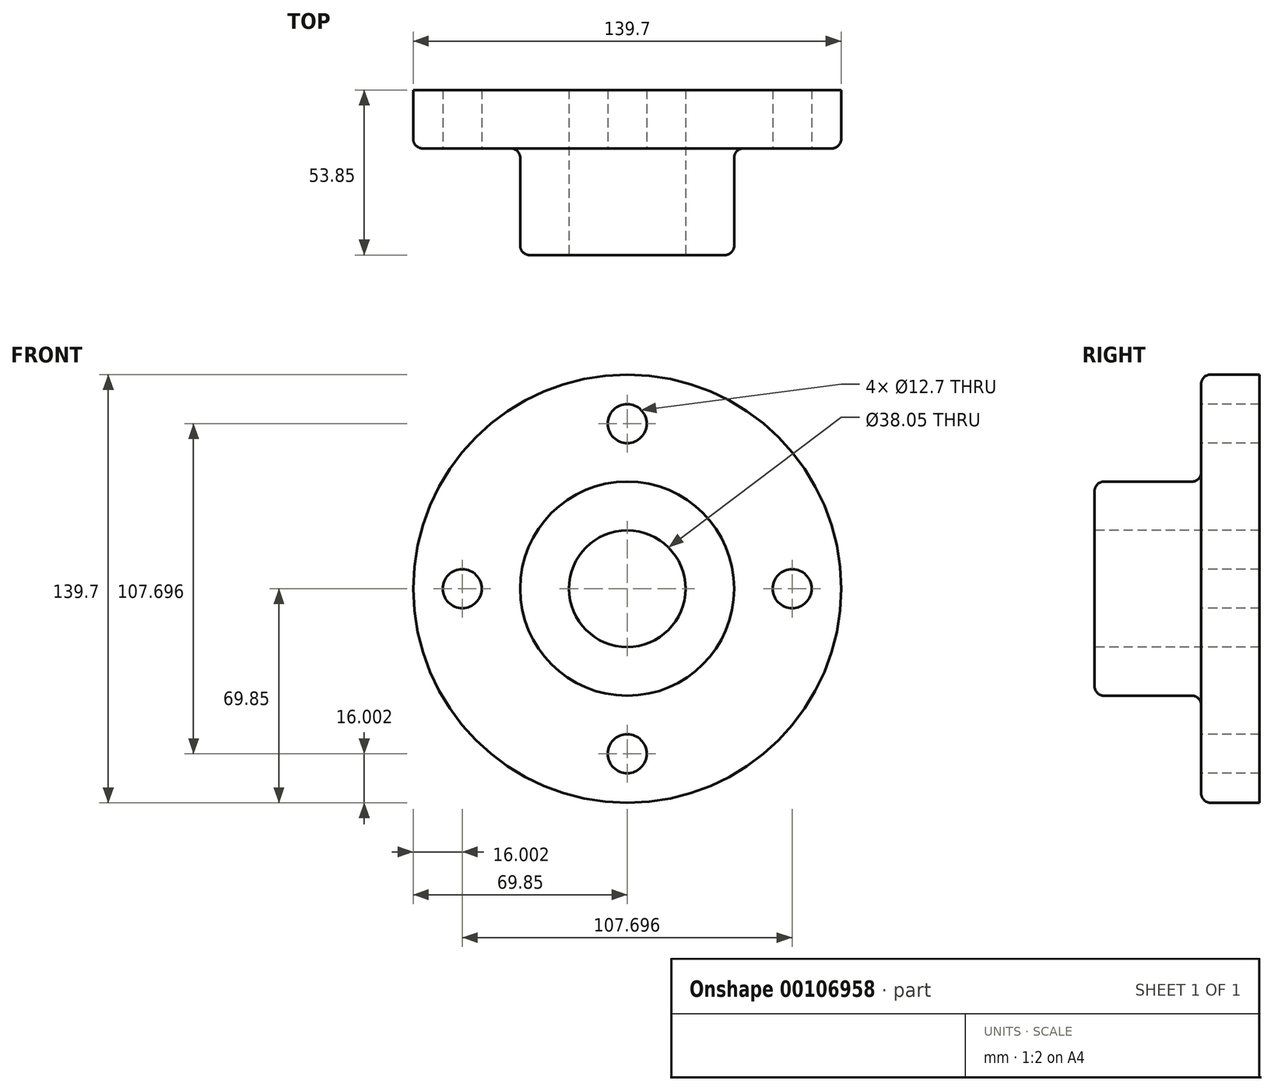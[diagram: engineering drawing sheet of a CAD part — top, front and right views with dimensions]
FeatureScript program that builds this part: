
annotation { "Feature Type Name" : "Feature", "Feature Type Description" : "" }
export const myFeature = defineFeature(function(context is Context, id is Id, definition is map)
    precondition{}
    {
        {
            var Q0;
            Q0=qCreatedBy(makeId("Right.planeOp"),FACE);
            var sketch = newSketch(context, id + "F0", { "sketchPlane" : qUnion([Q0])});
            skLineSegment(sketch, "E0", {"start": v(0, 0) * mm, "end": v(53.85, 0) * mm});
            skLineSegment(sketch, "E1", {"start": v(53.85, 0) * mm, "end": v(53.85, 69.85) * mm});
            skLineSegment(sketch, "E2", {"start": v(53.85, 69.85) * mm, "end": v(34.8, 69.85) * mm});
            skLineSegment(sketch, "E3", {"start": v(34.8, 69.85) * mm, "end": v(34.8, 34.93) * mm});
            skLineSegment(sketch, "E4", {"start": v(34.8, 34.93) * mm, "end": v(0, 34.93) * mm});
            skLineSegment(sketch, "E5", {"start": v(0, 34.93) * mm, "end": v(0, 0) * mm});
            skSolve(sketch);
        }
        {
            var Q0;
            Q0=makeQuery(id+"F0.imprint","IMPRINT",FACE,{"disambiguationData":[TD([[makeQuery(id+"F0.imprint","IMPRINT",EDGE,{"derivedFrom":sQuery(id+"F0.wireOp",EDGE,"E0")}),1.0]])]});
            var Q1;
            Q1=sQuery(id+"F0.wireOp",EDGE,"E0");
            revolve(context, id + "F1", {"entities" : qUnion([Q0]), "axis" : qUnion([Q1]), "revolveType" : RevolveType.FULL});
        }
        {
            var Q0;
            Q0=makeQuery(id+"F1.opRevolve","SWEPT_FACE",FACE,{"disambiguationData":[OSD([sQuery(id+"F0.wireOp",EDGE,"E5")])]});
            var sketch = newSketch(context, id + "F2", { "sketchPlane" : qUnion([Q0])});
            skCircle(sketch, "E6", {"center": v(0, 0) * mm, "radius": 19.02 * mm});
            skSolve(sketch);
        }
        {
            var Q0;
            Q0 = qSketchRegion(id + "F2", true);
            var Q1;
            Q1 = qSketchRegion(id + "F4", true);
            extrude(context, id + "F3", {"entities" : qUnion([Q0, Q1]), "operationType" : NewBodyOperationType.REMOVE, "endBound" : BoundingType.THROUGH_ALL, "oppositeDirection" : true, "depth" : 25 * mm});
        }
        {
            var Q0;
            Q0=makeQuery(id+"F1.opRevolve","SWEPT_FACE",FACE,{"disambiguationData":[OSD([sQuery(id+"F0.wireOp",EDGE,"E3")])]});
            var sketch = newSketch(context, id + "F4", { "sketchPlane" : qUnion([Q0])});
            skCircle(sketch, "E7", {"center": v(0, 0) * mm, "radius": 53.85 * mm, "construction": true});
            skCircle(sketch, "E8", {"center": v(0, 53.85) * mm, "radius": 6.35 * mm});
            skCircle(sketch, "E9", {"center": v(-53.85, 0) * mm, "radius": 6.35 * mm});
            skCircle(sketch, "E10", {"center": v(0, -53.85) * mm, "radius": 6.35 * mm});
            skCircle(sketch, "E11", {"center": v(53.85, 0) * mm, "radius": 6.35 * mm});
            skSolve(sketch);
        }
        {
            var Q0;
            Q0=makeQuery(id+"F4.imprint","IMPRINT",FACE,{"disambiguationData":[TD([[makeQuery(id+"F4.imprint","IMPRINT",EDGE,{"derivedFrom":sQuery(id+"F4.wireOp",EDGE,"E8")}),1.0]])]});
            var Q1;
            Q1=makeQuery(id+"F4.imprint","IMPRINT",FACE,{"disambiguationData":[TD([[makeQuery(id+"F4.imprint","IMPRINT",EDGE,{"derivedFrom":sQuery(id+"F4.wireOp",EDGE,"E9")}),1.0]])]});
            var Q2;
            Q2=makeQuery(id+"F4.imprint","IMPRINT",FACE,{"disambiguationData":[TD([[makeQuery(id+"F4.imprint","IMPRINT",EDGE,{"derivedFrom":sQuery(id+"F4.wireOp",EDGE,"E11")}),1.0]])]});
            var Q3;
            Q3=makeQuery(id+"F4.imprint","IMPRINT",FACE,{"disambiguationData":[TD([[makeQuery(id+"F4.imprint","IMPRINT",EDGE,{"derivedFrom":sQuery(id+"F4.wireOp",EDGE,"E10")}),1.0]])]});
            extrude(context, id + "F5", {"entities" : qUnion([Q0, Q1, Q2, Q3]), "operationType" : NewBodyOperationType.REMOVE, "endBound" : BoundingType.THROUGH_ALL, "oppositeDirection" : true, "depth" : 25 * mm});
        }
        {
            var Q0;
            Q0=makeQuery(id+"F1.opRevolve","SWEPT_EDGE",EDGE,{"disambiguationData":[OSD([sQuery(id+"F0.wireOp",EDGE,"E3"),sQuery(id+"F0.wireOp",EDGE,"E4")])]});
            var Q1;
            Q1=makeQuery(id+"F1.opRevolve","SWEPT_EDGE",EDGE,{"disambiguationData":[OSD([sQuery(id+"F0.wireOp",EDGE,"E4"),sQuery(id+"F0.wireOp",EDGE,"E5")])]});
            var Q2;
            Q2=makeQuery(id+"F1.opRevolve","SWEPT_EDGE",EDGE,{"disambiguationData":[OSD([sQuery(id+"F0.wireOp",EDGE,"E2"),sQuery(id+"F0.wireOp",EDGE,"E3")])]});
            fillet(context, id + "F6", {"entities" : qUnion([Q0, Q1, Q2]), "radius" : 3.05 * mm, "tangentPropagation" : true, "allowEdgeOverflow" : false});
        }
    });
